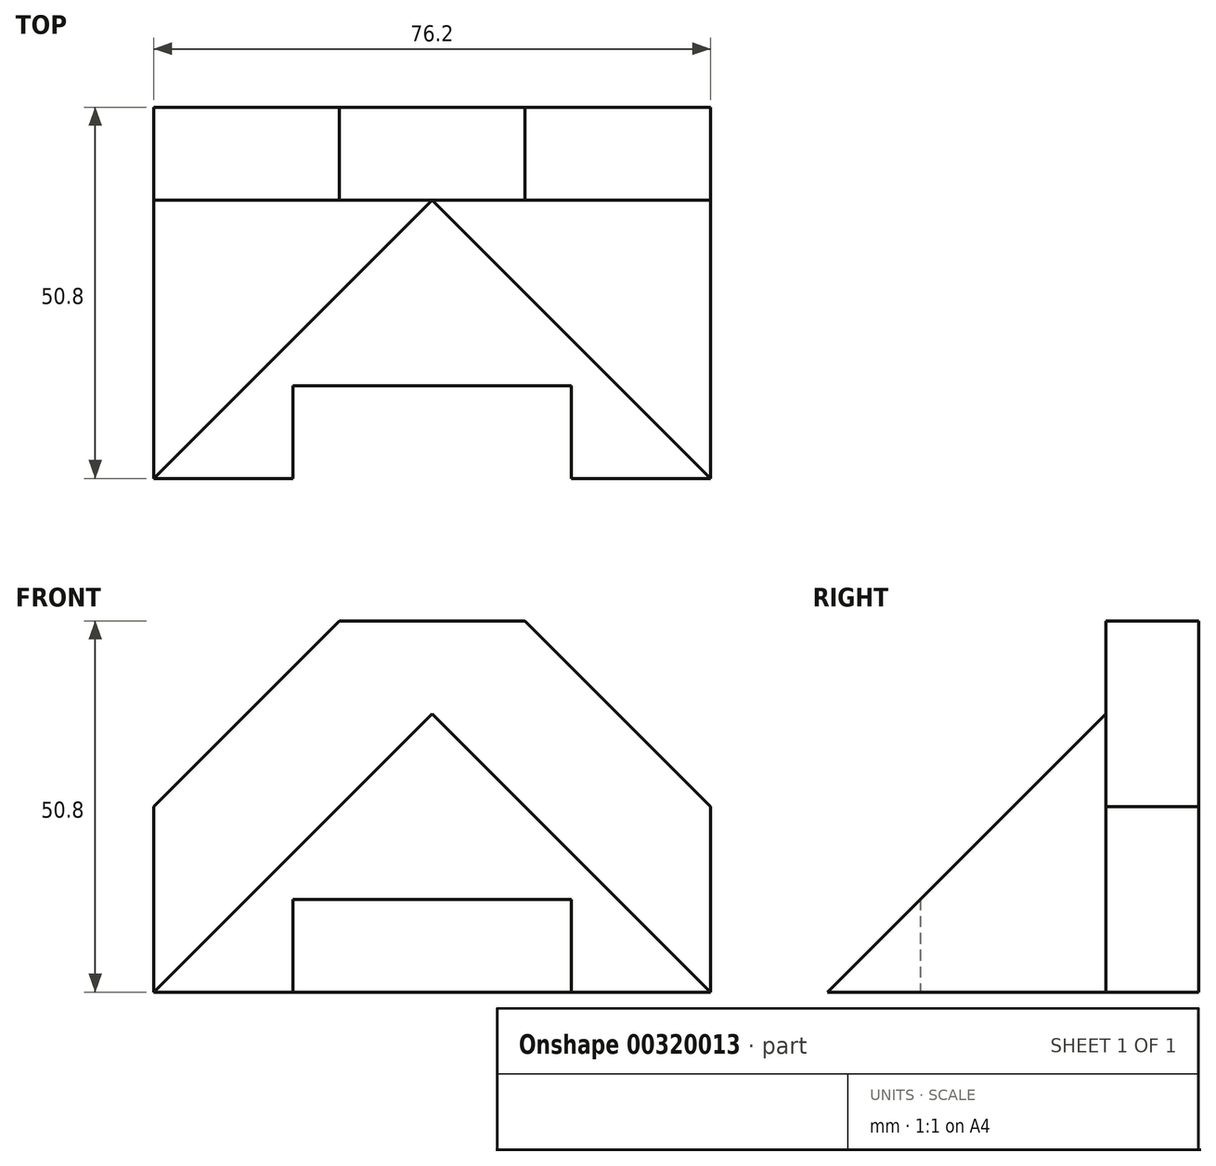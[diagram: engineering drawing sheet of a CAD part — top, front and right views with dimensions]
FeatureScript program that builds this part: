
annotation { "Feature Type Name" : "Feature", "Feature Type Description" : "" }
export const myFeature = defineFeature(function(context is Context, id is Id, definition is map)
    precondition{}
    {
        {
            var Q0;
            Q0=qCreatedBy(makeId("Top.planeOp"),FACE);
            var sketch = newSketch(context, id + "F0", { "sketchPlane" : qUnion([Q0])});
            skLineSegment(sketch, "E0.bottom", {"start": v(-23.4, 37.3) * mm, "end": v(52.8, 37.3) * mm});
            skLineSegment(sketch, "E0.top", {"start": v(-23.4, -13.5) * mm, "end": v(52.8, -13.5) * mm});
            skLineSegment(sketch, "E0.left", {"start": v(-23.4, 37.3) * mm, "end": v(-23.4, -13.5) * mm});
            skLineSegment(sketch, "E0.right", {"start": v(52.8, 37.3) * mm, "end": v(52.8, -13.5) * mm});
            skSolve(sketch);
        }
        {
            var Q0;
            Q0 = qSketchRegion(id + "F0", true);
            extrude(context, id + "F1", {"entities" : qUnion([Q0]), "depth" : 50.8 * mm});
        }
        {
            var Q0;
            Q0=makeQuery(id+"F1.opExtrude","SWEPT_FACE",FACE,{"disambiguationData":[OSD([sQuery(id+"F0.wireOp",EDGE,"E0.top")])]});
            var sketch = newSketch(context, id + "F2", { "sketchPlane" : qUnion([Q0])});
            skLineSegment(sketch, "E1", {"start": v(14.7, 38.1) * mm, "end": v(52.8, 0) * mm});
            skLineSegment(sketch, "E2", {"start": v(52.8, 0) * mm, "end": v(52.8, 38.1) * mm});
            skLineSegment(sketch, "E3", {"start": v(52.8, 38.1) * mm, "end": v(14.7, 38.1) * mm});
            skSolve(sketch);
        }
        {
            var Q0;
            Q0 = qSketchRegion(id + "F2", true);
            extrude(context, id + "F3", {"entities" : qUnion([Q0]), "operationType" : NewBodyOperationType.REMOVE, "oppositeDirection" : true, "depth" : 38.1 * mm});
        }
        {
            var Q0;
            Q0=makeQuery(id+"F1.opExtrude","SWEPT_FACE",FACE,{"disambiguationData":[OSD([sQuery(id+"F0.wireOp",EDGE,"E0.top")])]});
            var sketch = newSketch(context, id + "F4", { "sketchPlane" : qUnion([Q0])});
            skLineSegment(sketch, "E4", {"start": v(14.7, 38.1) * mm, "end": v(-23.4, 0) * mm});
            skLineSegment(sketch, "E5", {"start": v(-23.4, 0) * mm, "end": v(-23.4, 38.1) * mm});
            skLineSegment(sketch, "E6", {"start": v(14.7, 38.1) * mm, "end": v(52.8, 38.1) * mm});
            skLineSegment(sketch, "E7", {"start": v(52.8, 38.1) * mm, "end": v(52.8, 50.8) * mm});
            skLineSegment(sketch, "E8", {"start": v(52.8, 50.8) * mm, "end": v(-23.4, 50.8) * mm});
            skLineSegment(sketch, "E9", {"start": v(-23.4, 50.8) * mm, "end": v(-23.4, 38.1) * mm});
            skSolve(sketch);
        }
        {
            var Q0;
            Q0=makeQuery(id+"FTiGzfGFzlZKyT2_1.boolean.opBoolean","MERGE",FACE,{"derivedFrom":[makeQuery(id+"F3.boolean.opBoolean","COPY",FACE,{"derivedFrom":makeQuery(id+"F3.opExtrude","CAP_FACE",FACE,{"disambiguationData":[OSD([sQuery(id+"F2.wireOp",EDGE,"E1"),sQuery(id+"F2.wireOp",EDGE,"E2"),sQuery(id+"F2.wireOp",EDGE,"E3")])],"isStart":false})}),makeQuery(id+"FTiGzfGFzlZKyT2_1.opExtrude","CAP_FACE",FACE,{"disambiguationData":[OSD([sQuery(id+"F4.wireOp",EDGE,"E4"),sQuery(id+"F4.wireOp",EDGE,"E5"),sQuery(id+"F4.wireOp",EDGE,"E6"),sQuery(id+"F4.wireOp",EDGE,"E7"),sQuery(id+"F4.wireOp",EDGE,"E8"),sQuery(id+"F4.wireOp",EDGE,"E9")])],"isStart":false})]});
            var sketch = newSketch(context, id + "F5", { "sketchPlane" : qUnion([Q0])});
            skLineSegment(sketch, "E10", {"start": v(-23.4, 50.8) * mm, "end": v(-23.4, 25.4) * mm});
            skLineSegment(sketch, "E11", {"start": v(-23.4, 25.4) * mm, "end": v(-23.4, 50.8) * mm});
            skLineSegment(sketch, "E12", {"start": v(-23.4, 50.8) * mm, "end": v(2, 50.8) * mm});
            skLineSegment(sketch, "E13", {"start": v(2, 50.8) * mm, "end": v(-23.4, 25.4) * mm});
            skLineSegment(sketch, "E14", {"start": v(52.8, 50.8) * mm, "end": v(27.4, 50.8) * mm});
            skLineSegment(sketch, "E15", {"start": v(52.8, 50.8) * mm, "end": v(52.8, 25.4) * mm});
            skLineSegment(sketch, "E16", {"start": v(52.8, 25.4) * mm, "end": v(27.4, 50.8) * mm});
            skSolve(sketch);
        }
        {
            var Q0;
            Q0 = qSketchRegion(id + "F5", true);
            extrude(context, id + "F6", {"entities" : qUnion([Q0]), "operationType" : NewBodyOperationType.REMOVE, "oppositeDirection" : true, "depth" : 25.4 * mm});
        }
        {
            var Q0;
            Q0=makeQuery(id+"F1.opExtrude","SWEPT_FACE",FACE,{"disambiguationData":[OSD([sQuery(id+"F0.wireOp",EDGE,"E0.left")])]});
            var sketch = newSketch(context, id + "F7", { "sketchPlane" : qUnion([Q0])});
            skLineSegment(sketch, "E17", {"start": v(13.5, 0) * mm, "end": v(13.5, 50.8) * mm});
            skLineSegment(sketch, "E18", {"start": v(13.5, 50.8) * mm, "end": v(-24.6, 50.8) * mm});
            skLineSegment(sketch, "E19", {"start": v(-24.6, 50.8) * mm, "end": v(-24.6, 38.1) * mm});
            skLineSegment(sketch, "E20", {"start": v(-24.6, 38.1) * mm, "end": v(13.5, 0) * mm});
            skSolve(sketch);
        }
        {
            var Q0;
            Q0 = qSketchRegion(id + "F7", true);
            extrude(context, id + "F8", {"entities" : qUnion([Q0]), "operationType" : NewBodyOperationType.REMOVE, "oppositeDirection" : true, "depth" : 76.2 * mm});
        }
        {
            var Q0;
            Q0 = qSketchRegion(id + "F4", true);
            extrude(context, id + "F9", {"entities" : qUnion([Q0]), "operationType" : NewBodyOperationType.REMOVE, "oppositeDirection" : true, "depth" : 38.1 * mm});
        }
        {
            var Q0;
            Q0=makeQuery(id+"F1.opExtrude","CAP_FACE",FACE,{"disambiguationData":[OSD([sQuery(id+"F0.wireOp",EDGE,"E0.bottom"),sQuery(id+"F0.wireOp",EDGE,"E0.top"),sQuery(id+"F0.wireOp",EDGE,"E0.left"),sQuery(id+"F0.wireOp",EDGE,"E0.right")])],"isStart":true});
            var sketch = newSketch(context, id + "F10", { "sketchPlane" : qUnion([Q0])});
            skLineSegment(sketch, "E21", {"start": v(14.7, 13.5) * mm, "end": v(33.74, 13.5) * mm});
            skLineSegment(sketch, "E22", {"start": v(33.74, 13.5) * mm, "end": v(33.74, 0.8) * mm});
            skLineSegment(sketch, "E23", {"start": v(33.74, 0.8) * mm, "end": v(-4.36, 0.8) * mm});
            skLineSegment(sketch, "E24", {"start": v(-4.36, 0.8) * mm, "end": v(-4.36, 13.5) * mm});
            skLineSegment(sketch, "E25", {"start": v(-4.36, 13.5) * mm, "end": v(14.7, 13.5) * mm});
            skSolve(sketch);
        }
        {
            var Q0;
            Q0 = qSketchRegion(id + "F10", true);
            extrude(context, id + "F11", {"entities" : qUnion([Q0]), "operationType" : NewBodyOperationType.REMOVE, "oppositeDirection" : true, "depth" : 12.7 * mm});
        }
    });
